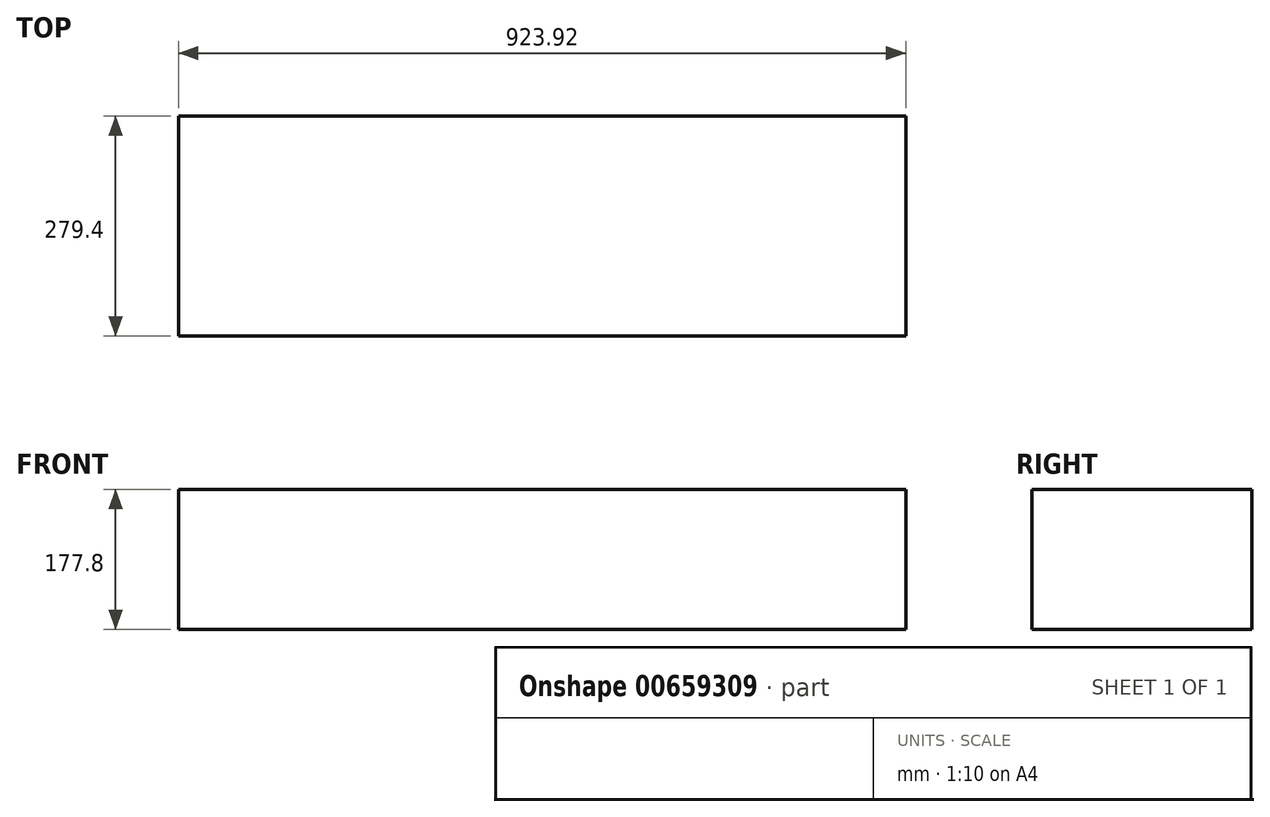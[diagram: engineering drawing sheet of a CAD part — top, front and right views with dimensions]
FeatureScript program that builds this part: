
annotation { "Feature Type Name" : "Feature", "Feature Type Description" : "" }
export const myFeature = defineFeature(function(context is Context, id is Id, definition is map)
    precondition{}
    {
        {
            var Q0;
            Q0=qCreatedBy(makeId("Top.planeOp"),FACE);
            var sketch = newSketch(context, id + "F0", { "sketchPlane" : qUnion([Q0])});
            skLineSegment(sketch, "E0.bottom", {"start": v(0, 0) * mm, "end": v(923.93, 0) * mm});
            skLineSegment(sketch, "E0.top", {"start": v(0, -279.4) * mm, "end": v(923.93, -279.4) * mm});
            skLineSegment(sketch, "E0.left", {"start": v(0, 0) * mm, "end": v(0, -279.4) * mm});
            skLineSegment(sketch, "E0.right", {"start": v(923.93, 0) * mm, "end": v(923.93, -279.4) * mm});
            skSolve(sketch);
        }
        {
            var Q0;
            Q0=makeQuery(id+"F0.imprint","IMPRINT",FACE,{"disambiguationData":[TD([[makeQuery(id+"F0.imprint","IMPRINT",EDGE,{"derivedFrom":sQuery(id+"F0.wireOp",EDGE,"E0.bottom")}),-1.0]])]});
            extrude(context, id + "F1", {"entities" : qUnion([Q0]), "depth" : 177.8 * mm, "offsetDistance" : 25.4 * mm});
        }
    });
